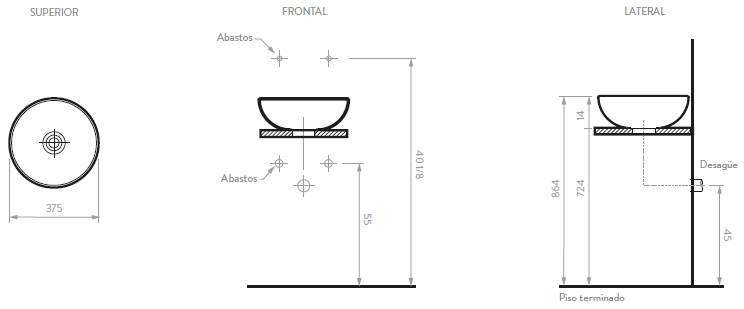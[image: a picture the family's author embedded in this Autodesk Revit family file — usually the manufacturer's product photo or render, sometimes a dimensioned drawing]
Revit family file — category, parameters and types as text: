
# Revit family: 147006811_Mueble Vital Vessel 60 cm a Piso con Lavamanos
name_source: partatom
category: Furniture
units: mm (PartAtom-declared; Revit-internal decimal feet)

## family parameters
Always vertical = Yes
Cut with Voids When Loaded = No
OmniClass Number = 23.31.13.11
OmniClass Title = Single Sinks
Room Calculation Point = No
Shared = No
Work Plane-Based = No

## types (1)
- 147006811_Mueble Vital Vessel 60 cm a Piso con Lavamanos
    Acabado = Corona_Madera_Blanco
    Alto = 750 mm  [stored 2.46063 ft]
    Ancho = 600 mm  [stored 1.9685 ft]
    Creado por = IDD
    Description = Mueble Vital con lavamanos Tipo Vessel a piso con diseño retro que combina
materiales, colores y texturas para dar armonía a tu baño.
· Repisa Interna para mayor orden y almacenamiento.
· Incluye patas niveladoras que por medio de giros permiten adaptar el
mueble a las superficies no uniformes.
· Resistentes a la humedad
· Compatible con diferentes lavamanos tipo Vessel.
    Fecha de creación = 30/07/2020
    Garantía = 5 Años de garantia (Madera)
    Garantía Herraje = 1 Años
    Longitud = 450 mm  [stored 1.47638 ft]
    Manija = Corona_Aluminio
    Manufacturer = Corona
    Material = Corona_Madera_Aglomerada_Miel
    Model = Vital Vessel 60
    Peso Bruto aprox = 41,0 lb (18,6 kg).
    Peso Neto aprox = 39,2 lb (17,8 kg).
    Resistencia a la humedad = 8%.
    Resistencia al rayado = 700 ciclos.
    URL = https://corona.co

note: [stored X ft] marks values corroborated as IEEE doubles in the binary element streams (Revit-internal decimal feet)

## geometry (parser evidence)
native form markers: Sweep x9
no freeform markers — native parametric forms only
